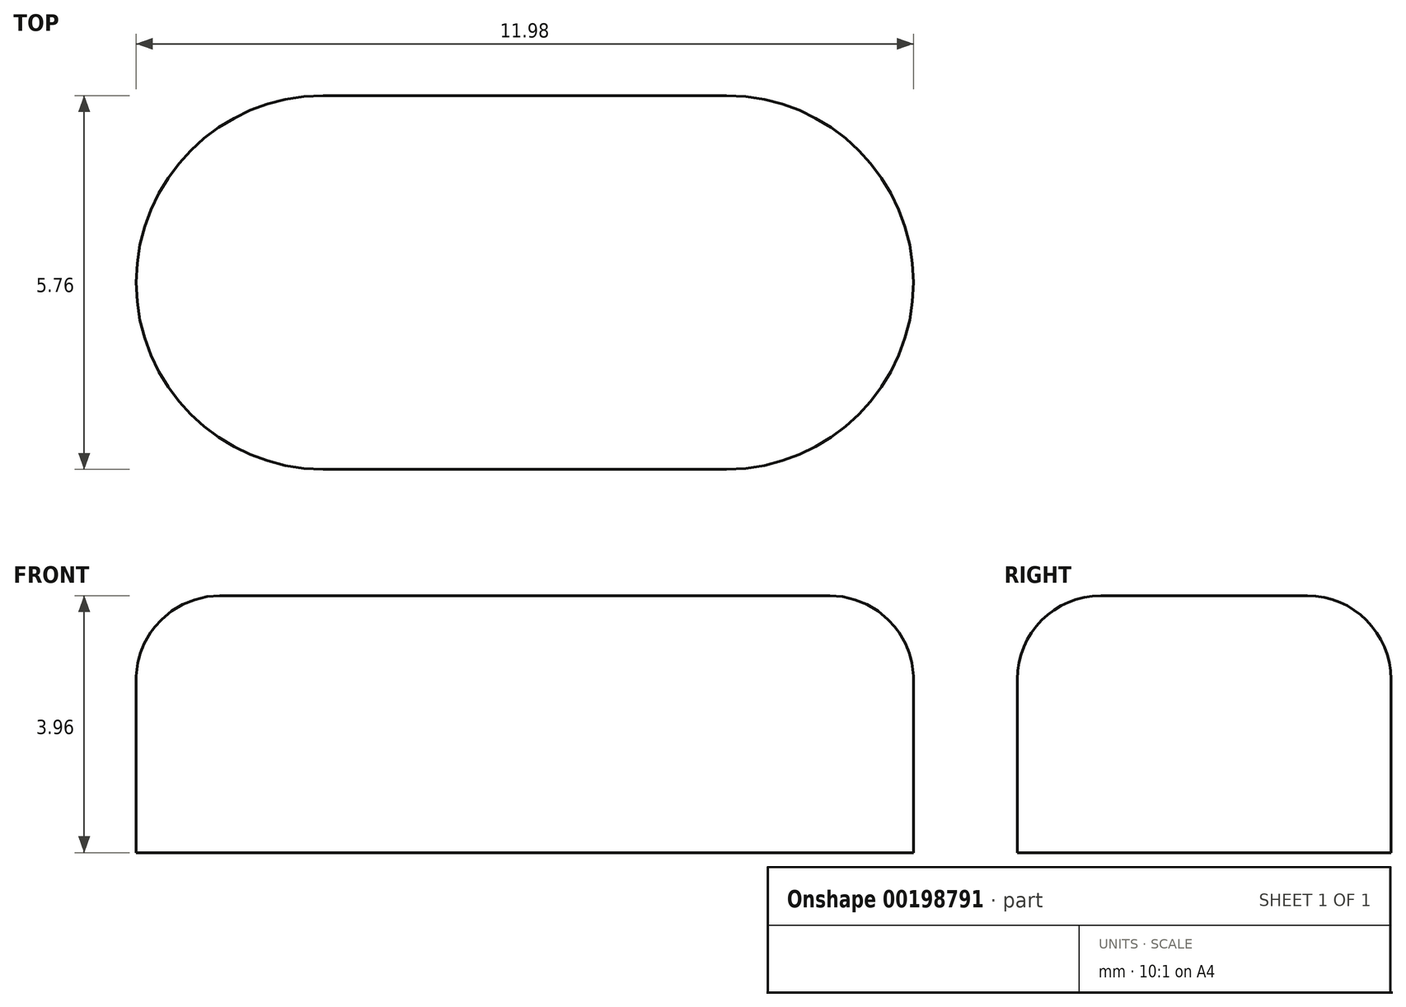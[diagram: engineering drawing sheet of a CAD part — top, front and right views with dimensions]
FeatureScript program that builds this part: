
annotation { "Feature Type Name" : "Feature", "Feature Type Description" : "" }
export const myFeature = defineFeature(function(context is Context, id is Id, definition is map)
    precondition{}
    {
        {
            var Q0;
            Q0=qCreatedBy(makeId("Top.planeOp"),FACE);
            var sketch = newSketch(context, id + "F0", { "sketchPlane" : qUnion([Q0])});
            skArc(sketch, "E0", {"start": v(-3.11, 2.88) * mm, "mid": v(-6, 0) * mm, "end": v(-3.11, -2.88) * mm});
            skArc(sketch, "E1", {"start": v(3.1, -2.88) * mm, "mid": v(6, 0) * mm, "end": v(3.11, 2.88) * mm});
            skLineSegment(sketch, "E2", {"start": v(-3.1, 0) * mm, "end": v(3.1, 0) * mm, "construction": true});
            skPoint(sketch, "E3", {"position": v(0, 0) * mm});
            skLineSegment(sketch, "E4", {"start": v(-3.1, 2.88) * mm, "end": v(3.11, 2.88) * mm});
            skLineSegment(sketch, "E5", {"start": v(3.1, -2.88) * mm, "end": v(-3.1, -2.88) * mm});
            skSolve(sketch);
        }
        {
            var Q0;
            Q0 = qSketchRegion(id + "F0", true);
            extrude(context, id + "F1", {"entities" : qUnion([Q0]), "depth" : 1.29 * mm, "hasSecondDirection" : true, "secondDirectionOppositeDirection" : true, "secondDirectionDepth" : (2.92 - 0.25) * mm});
        }
        {
            var Q0;
            Q0=makeQuery(id+"F1.opExtrude","CAP_EDGE",EDGE,{"disambiguationData":[OSD([sQuery(id+"F0.wireOp",EDGE,"E1")])],"isStart":false});
            var Q1;
            Q1=makeQuery(id+"F1.opExtrude","CAP_EDGE",EDGE,{"disambiguationData":[OSD([sQuery(id+"F0.wireOp",EDGE,"E4")])],"isStart":false});
            var Q2;
            Q2=makeQuery(id+"F1.opExtrude","CAP_EDGE",EDGE,{"disambiguationData":[OSD([sQuery(id+"F0.wireOp",EDGE,"E5")])],"isStart":false});
            var Q3;
            Q3=makeQuery(id+"F1.opExtrude","CAP_EDGE",EDGE,{"disambiguationData":[OSD([sQuery(id+"F0.wireOp",EDGE,"E0")])],"isStart":false});
            fillet(context, id + "F2", {"entities" : qUnion([Q0, Q1, Q2, Q3]), "radius" : 1.29 * mm, "tangentPropagation" : true, "allowEdgeOverflow" : false});
        }
    });
